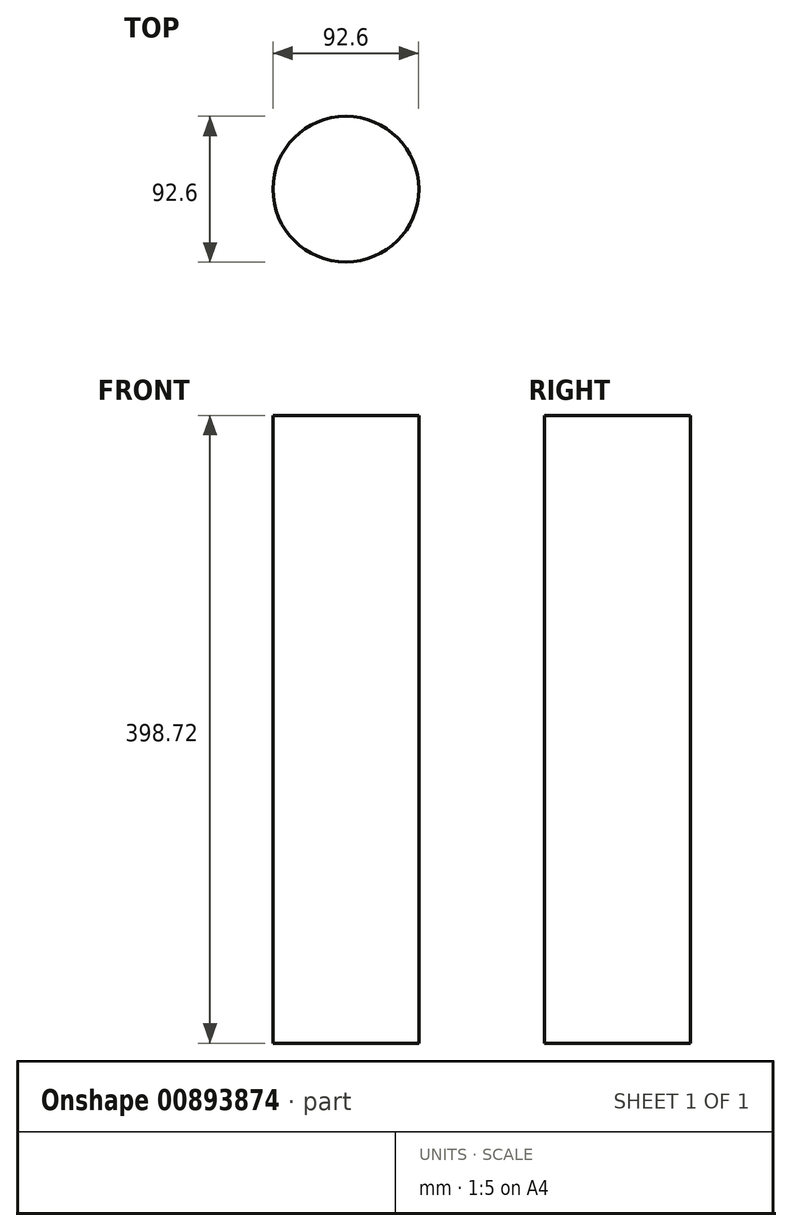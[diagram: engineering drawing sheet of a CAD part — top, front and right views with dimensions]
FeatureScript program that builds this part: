
annotation { "Feature Type Name" : "Feature", "Feature Type Description" : "" }
export const myFeature = defineFeature(function(context is Context, id is Id, definition is map)
    precondition{}
    {
        {
            var Q0;
            Q0=qCreatedBy(makeId("Top.planeOp"),FACE);
            var sketch = newSketch(context, id + "F0", { "sketchPlane" : qUnion([Q0])});
            skCircle(sketch, "E0", {"center": v(0, 0) * mm, "radius": 76.48 * mm});
            skCircle(sketch, "E1", {"center": v(0, 0) * mm, "radius": 46.3 * mm});
            skSolve(sketch);
        }
        {
            var Q0;
            Q0=makeQuery(id+"F0.imprint","IMPRINT",FACE,{"disambiguationData":[TD([[makeQuery(id+"F0.imprint","IMPRINT",EDGE,{"derivedFrom":sQuery(id+"F0.wireOp",EDGE,"E1")}),1.0]])]});
            extrude(context, id + "F1", {"entities" : qUnion([Q0]), "depth" : 398.72 * mm, "offsetDistance" : 25.4 * mm});
        }
    });
